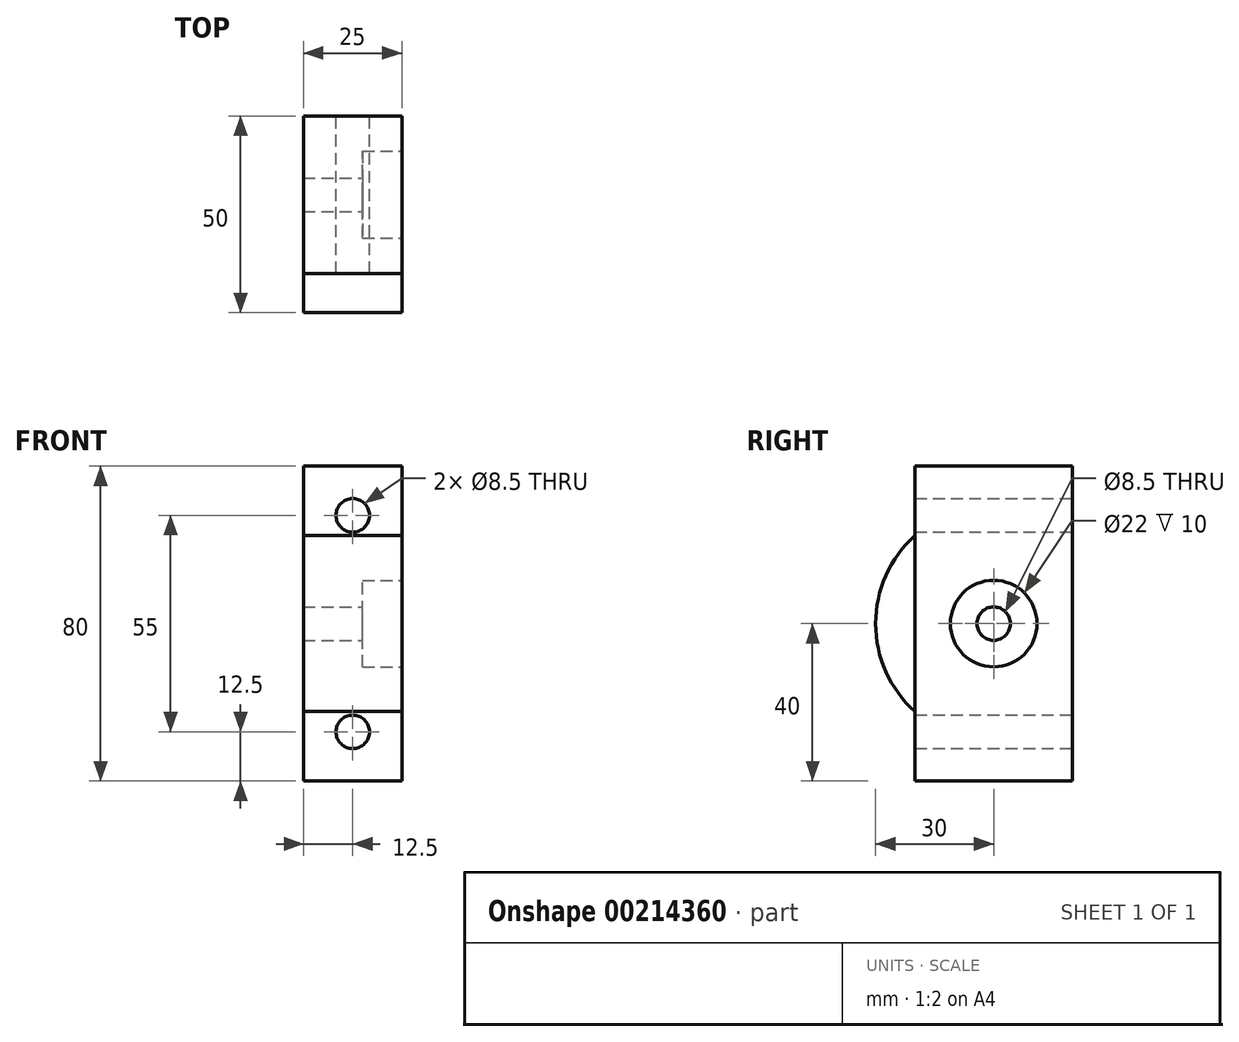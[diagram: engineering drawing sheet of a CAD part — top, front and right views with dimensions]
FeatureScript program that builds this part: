
annotation { "Feature Type Name" : "Feature", "Feature Type Description" : "" }
export const myFeature = defineFeature(function(context is Context, id is Id, definition is map)
    precondition{}
    {
        {
            var Q0;
            Q0=qCreatedBy(makeId("Front.planeOp"),FACE);
            var sketch = newSketch(context, id + "F0", { "sketchPlane" : qUnion([Q0])});
            skLineSegment(sketch, "E0.bottom", {"start": v(12.5, 40) * mm, "end": v(-12.5, 40) * mm});
            skLineSegment(sketch, "E0.top", {"start": v(12.5, -40) * mm, "end": v(-12.5, -40) * mm});
            skLineSegment(sketch, "E0.left", {"start": v(12.5, 40) * mm, "end": v(12.5, -40) * mm});
            skLineSegment(sketch, "E0.right", {"start": v(-12.5, 40) * mm, "end": v(-12.5, -40) * mm});
            skPoint(sketch, "E0.middle", {"position": v(0, 0) * mm});
            skCircle(sketch, "E1", {"center": v(0, 27.5) * mm, "radius": 4.25 * mm});
            skCircle(sketch, "E2", {"center": v(0, -27.5) * mm, "radius": 4.25 * mm});
            skSolve(sketch);
        }
        {
            var Q0;
            Q0=qSketchRegion(id+"F0",true);
            extrude(context, id + "F1", {"entities" : qUnion([Q0]), "depth" : 20 * mm, "hasSecondDirection" : true, "secondDirectionOppositeDirection" : true, "secondDirectionDepth" : 20 * mm});
        }
        {
            var Q0;
            Q0=qCreatedBy(makeId("Right.planeOp"),FACE);
            var sketch = newSketch(context, id + "F2", { "sketchPlane" : qUnion([Q0])});
            skCircle(sketch, "E3", {"center": v(0, 0) * mm, "radius": 4.25 * mm});
            skSolve(sketch);
        }
        {
            var Q0;
            Q0=qSketchRegion(id+"F2",true);
            extrude(context, id + "F3", {"entities" : qUnion([Q0]), "operationType" : NewBodyOperationType.REMOVE, "endBound" : BoundingType.UP_TO_NEXT, "oppositeDirection" : true, "depth" : 25 * mm});
        }
        {
            var Q0;
            Q0=makeQuery(id+"F1.opExtrude","SWEPT_FACE",FACE,{"disambiguationData":[OSD([sQuery(id+"F0.wireOp",EDGE,"E0.left")])]});
            var sketch = newSketch(context, id + "F4", { "sketchPlane" : qUnion([Q0])});
            skCircle(sketch, "E4", {"center": v(0, 0) * mm, "radius": 11 * mm});
            skSolve(sketch);
        }
        {
            var Q0;
            Q0=qSketchRegion(id+"F4",true);
            extrude(context, id + "F5", {"entities" : qUnion([Q0]), "operationType" : NewBodyOperationType.REMOVE, "oppositeDirection" : true, "depth" : 10 * mm});
        }
        {
            var Q0;
            Q0=makeQuery(id+"F1.opExtrude","SWEPT_FACE",FACE,{"disambiguationData":[OSD([sQuery(id+"F0.wireOp",EDGE,"E0.left")])]});
            var sketch = newSketch(context, id + "F6", { "sketchPlane" : qUnion([Q0])});
            skCircle(sketch, "E5", {"center": v(0, 0) * mm, "radius": 4.25 * mm});
            skSolve(sketch);
        }
        {
            var Q0;
            Q0=qSketchRegion(id+"F6",true);
            extrude(context, id + "F7", {"entities" : qUnion([Q0]), "operationType" : NewBodyOperationType.REMOVE, "oppositeDirection" : true, "depth" : 25 * mm});
        }
        {
            var Q0;
            Q0=makeQuery(id+"F1.opExtrude","SWEPT_FACE",FACE,{"disambiguationData":[OSD([sQuery(id+"F0.wireOp",EDGE,"E0.right")])]});
            var sketch = newSketch(context, id + "F8", { "sketchPlane" : qUnion([Q0])});
            skArc(sketch, "E6", {"start": v(20, -22.36) * mm, "mid": v(30, 0) * mm, "end": v(20, 22.36) * mm});
            skLineSegment(sketch, "E7.0", {"start": v(20, 22.36) * mm, "end": v(20, -22.36) * mm});
            skPoint(sketch, "E8.orphan", {"position": v(20, 40) * mm});
            skPoint(sketch, "E9.orphan", {"position": v(20, -40) * mm});
            skSolve(sketch);
        }
        {
            var Q0;
            Q0 = qSketchRegion(id + "F8", true);
            extrude(context, id + "F9", {"entities" : qUnion([Q0]), "oppositeDirection" : true, "depth" : 25 * mm});
        }
    });
